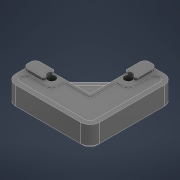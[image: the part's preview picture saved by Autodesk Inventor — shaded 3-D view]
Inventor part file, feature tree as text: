
AUTODESK INVENTOR PART (.ipt)
format: ipt  version: 2022.1 (Build 261234020, 234B)  size: 939,008 bytes
history: native  units: mm
features: move_body x16, projected_geometry x15, direct_edit x14, extrude x10, fillet x9, sketch x9, delete_face x6, chamfer x4, plane x1, other x1
ambient origin geometry x8: Origin, YZ Plane, XZ Plane, XY Plane, X Axis, Y Axis, Z Axis, Center Point
bodies: Volumenkörper1 (feature_tree)
feature tree (85):
  direct_edit  "Direktbearbeitung1"
  direct_edit  "Direktbearbeitung2"
  delete_face  "Fläche löschen1"
  extrude  "Extrusion1"  Depth=0.5mm TaperAngle=0.0deg
  fillet  "Rundung1"  Radius=0.5mm
  fillet  "Rundung2"  Radius=6.0mm
  extrude  "Extrusion2"  Depth=0.5mm
  fillet  "Rundung3"  Radius=1.0mm
  extrude  "Extrusion3"  Depth=2.0mm
  delete_face  "Fläche löschen2"
  extrude  "Extrusion4"  Depth=20.0mm
  direct_edit  "Direktbearbeitung3"
  extrude  "Extrusion5"  Depth=1.0mm
  chamfer  "Fase3"  Distance=1.0mm
  plane  "Arbeitsebene1"
  extrude  "Extrusion6"  Depth=1.0mm
  direct_edit  "Direktbearbeitung4"
  direct_edit  "Direktbearbeitung5"
  chamfer  "Fase5"  Distance=0.2mm
  direct_edit  "Direktbearbeitung6"
  chamfer  "Fase6"  Distance=0.2mm
  direct_edit  "Direktbearbeitung8"
  delete_face  "Fläche löschen4"
  direct_edit  "Direktbearbeitung9"
  fillet  "Rundung4"  [1 undecoded]
  fillet  "Rundung5"  Radius=1.6mm
  fillet  "Rundung6"  Radius=0.2mm
  delete_face  "Fläche löschen5"
  delete_face  "Fläche löschen6"
  extrude  "Extrusion7"  Depth=2.0mm TaperAngle=45.0deg
  fillet  "Rundung7"  Radius=16.4mm
  direct_edit  "Direktbearbeitung10"
  sketch  "Skizze8"  dims[d22=1.0mm]
  extrude  "Extrusion8"  Depth=0.8mm
  extrude  "Extrusion9"  Depth=0.8mm
  chamfer  "Fase7"  Distance=7.6mm
  direct_edit  "Direktbearbeitung11"
  extrude  "Extrusion10"  Depth=2.0mm
  fillet  "Rundung8"  Radius=0.8mm
  direct_edit  "Direktbearbeitung12"
  direct_edit  "Direktbearbeitung13"
  fillet  "Rundung9"  Radius=0.8mm
  direct_edit  "Direktbearbeitung14"
  delete_face  "Fläche löschen7"
  direct_edit  "Direktbearbeitung15"
  sketch  "Skizze1"  dims[d0=0.0mm d1=0.0mm d2=1.4mm d3=0.0mm d4=0.0mm d5=5.4mm d6=0.5mm d7=6.0mm]
  projected_geometry  "Projizierte Kontur1"
  sketch  "Skizze2"  dims[d8=6.0mm d9=0.5mm d10=1.0mm d11=0.0mm]
  projected_geometry  "Projizierte Kontur2"
  projected_geometry  "Projizierte Kontur3"
  sketch  "Skizze3"  dims[d12=0.8mm d13=2.0mm]
  projected_geometry  "Projizierte Kontur4"
  sketch  "Skizze4"  dims[d14=20.0mm d15=20.0mm]
  projected_geometry  "Projizierte Kontur5"
  projected_geometry  "Projizierte Kontur6"
  sketch  "Skizze5"  dims[d16=1.0mm d17=0.0mm d18=1.0mm]
  projected_geometry  "Projizierte Kontur7"
  sketch  "Skizze6"  dims[d20=4.0mm]
  projected_geometry  "Projizierte Kontur8"
  sketch  "Skizze7"  dims[d21=4.0mm]
  projected_geometry  "Projizierte Kontur9"
  projected_geometry  "Projizierte Kontur10"
  projected_geometry  "Projizierte Kontur11"
  projected_geometry  "Projizierte Kontur12"
  projected_geometry  "Projizierte Kontur13"
  sketch  "Skizze9"  dims[d23=1.0mm d24=1.0mm d25=1.0mm d26=0.2mm d27=0.0mm d28=0.2mm d29=0.0mm d30=0.0mm d31=0.0mm d32=-1.6mm d39=1.6mm d40=0.2mm d41=0.0mm d42=0.2mm d43=2.0mm d44=45.0deg d45=16.4mm d46=0.8mm d47=0.8mm d48=7.6mm d49=7.6mm d50=0.8mm d51=0.8mm d52=0.4mm d53=0.4mm d54=3.0mm d55=3.8mm d56=0.6mm d57=0.0mm d58=18.4mm d59=0.0mm d60=0.0mm d61=0.6mm d62=0.0mm d63=0.0mm d64=-0.6mm d68=1.2mm d69=2.0mm d70=45.0deg d71=0.0mm d72=0.0mm d73=-0.2mm d74=0.2mm d75=2.0mm d76=45.0deg d80=0.0mm d81=0.0mm d82=1.9mm d83=0.0mm d84=0.0mm d85=-3.0mm d86=0.0mm d87=0.0mm d88=-3.0mm d89=1.0mm d90=2.0mm d91=1.0mm d92=0.8mm d93=0.8mm d94=4.0mm d95=4.0mm d96=4.0mm d97=4.0mm d98=2.0mm d99=10.0mm d100=0.0mm d101=1.0mm d102=0.0mm d103=0.0mm d104=0.8mm d105=0.0mm d106=0.0mm d107=0.8mm d108=1.6mm d109=4.8mm d111=6.4mm d112=4.8mm d113=6.4mm d114=10.0mm d115=0.0mm d116=10.0mm d117=0.0mm d118=0.2mm d119=2.0mm d120=45.0deg d121=0.0mm d122=0.0mm d123=0.2mm d124=8.0mm d125=0.8mm d126=0.8mm d127=8.0mm d128=10.0mm d129=0.0mm d130=0.8mm d131=0.0mm d132=0.0mm d133=-0.5mm d134=0.0mm d135=0.0mm d136=-0.5mm d137=0.5mm d138=0.0mm d139=0.0mm d140=0.2mm d141=0.0mm d142=0.0mm d143=2.0mm]
  projected_geometry  "Projizierte Kontur14"
  projected_geometry  "Projizierte Kontur15"
  other  "corner_panel_clip_4mm_x8"
  move_body  "Verschieben1"
  move_body  "Verschieben2"
  move_body  "Verschieben3"
  move_body  "Verschieben4"
  move_body  "Verschieben5"
  move_body  "Verschieben6"
  move_body  "Verschieben8"
  move_body  "Verschieben9"
  move_body  "Verschieben10"
  move_body  "Verschieben11"
  move_body  "Verschieben12"
  move_body  "Verschieben13"
  move_body  "Verschieben14"
  move_body  "Verschieben15"
  move_body  "Verschieben16"
  move_body  "Verschieben17"
note: 1 required parameter value undecoded (feature->parameter linkage not recoverable at this tier; creation-order binding heuristic only, values carry confidence <= 0.55)
